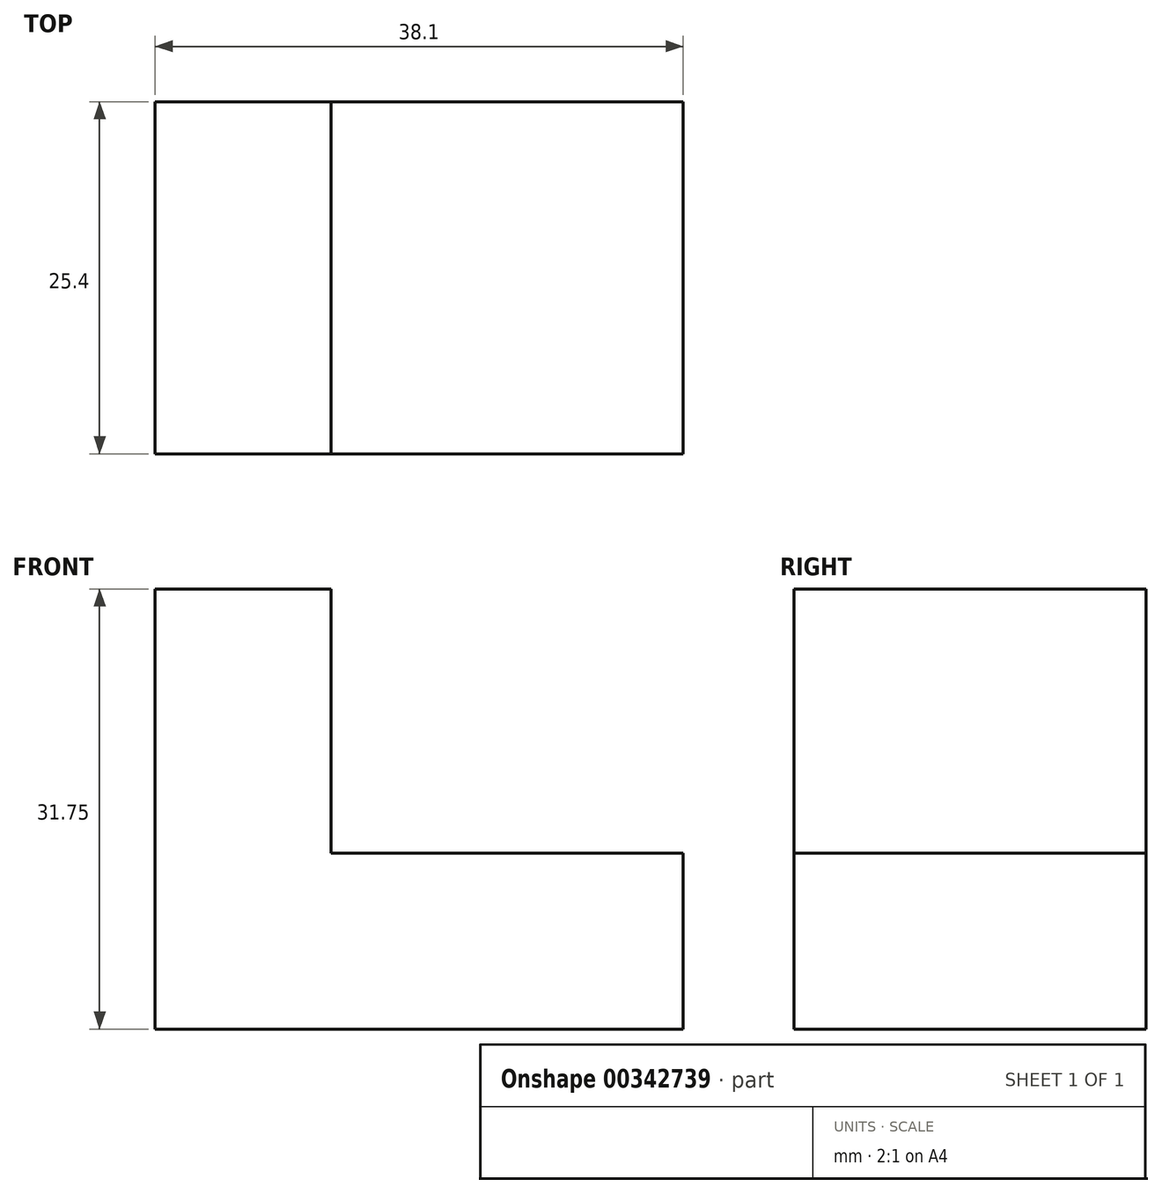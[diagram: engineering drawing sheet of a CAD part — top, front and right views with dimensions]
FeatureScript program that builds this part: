
annotation { "Feature Type Name" : "Feature", "Feature Type Description" : "" }
export const myFeature = defineFeature(function(context is Context, id is Id, definition is map)
    precondition{}
    {
        {
            var Q0;
            Q0=qCreatedBy(makeId("Front.planeOp"),FACE);
            var sketch = newSketch(context, id + "F0", { "sketchPlane" : qUnion([Q0])});
            skLineSegment(sketch, "E0", {"start": v(0, 0) * mm, "end": v(0, 31.75) * mm});
            skLineSegment(sketch, "E1", {"start": v(0, 31.75) * mm, "end": v(12.7, 31.75) * mm});
            skLineSegment(sketch, "E2", {"start": v(12.7, 31.75) * mm, "end": v(12.7, 12.7) * mm});
            skLineSegment(sketch, "E3", {"start": v(12.7, 12.7) * mm, "end": v(38.1, 12.7) * mm});
            skLineSegment(sketch, "E4", {"start": v(38.1, 12.7) * mm, "end": v(38.1, 0) * mm});
            skLineSegment(sketch, "E5", {"start": v(38.1, 0) * mm, "end": v(0, 0) * mm});
            skSolve(sketch);
        }
        {
            var Q0;
            Q0 = qSketchRegion(id + "F0", true);
            extrude(context, id + "F1", {"entities" : qUnion([Q0]), "depth" : 25.4 * mm});
        }
    });
